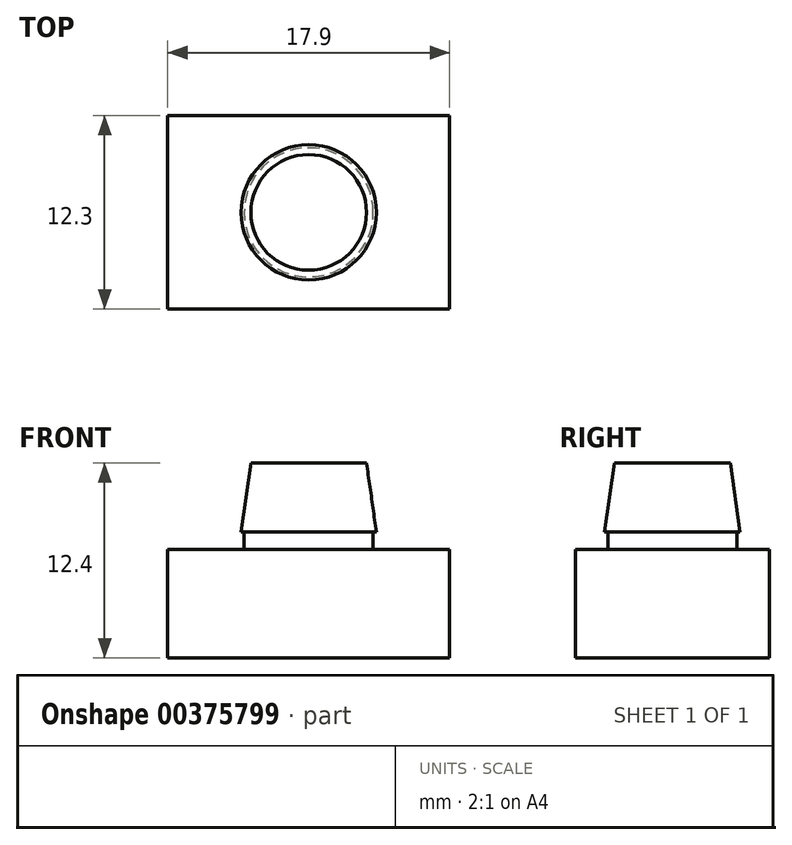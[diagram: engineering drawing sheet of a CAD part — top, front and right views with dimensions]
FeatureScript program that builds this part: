
annotation { "Feature Type Name" : "Feature", "Feature Type Description" : "" }
export const myFeature = defineFeature(function(context is Context, id is Id, definition is map)
    precondition{}
    {
        {
            var Q0;
            Q0=qCreatedBy(makeId("Top.planeOp"),FACE);
            var sketch = newSketch(context, id + "F0", { "sketchPlane" : qUnion([Q0])});
            skLineSegment(sketch, "E0.bottom", {"start": v(8.95, 6.15) * mm, "end": v(-8.95, 6.15) * mm});
            skLineSegment(sketch, "E0.top", {"start": v(8.95, -6.15) * mm, "end": v(-8.95, -6.15) * mm});
            skLineSegment(sketch, "E0.left", {"start": v(8.95, 6.15) * mm, "end": v(8.95, -6.15) * mm});
            skLineSegment(sketch, "E0.right", {"start": v(-8.95, 6.15) * mm, "end": v(-8.95, -6.15) * mm});
            skPoint(sketch, "E0.middle", {"position": v(0, 0) * mm});
            skSolve(sketch);
        }
        {
            var Q0;
            Q0 = qSketchRegion(id + "F0", true);
            extrude(context, id + "F1", {"entities" : qUnion([Q0]), "depth" : 6.9 * mm});
        }
        {
            var Q0;
            Q0=makeQuery(id+"F1.opExtrude","CAP_FACE",FACE,{"disambiguationData":[OSD([sQuery(id+"F0.wireOp",EDGE,"E0.bottom"),sQuery(id+"F0.wireOp",EDGE,"E0.top"),sQuery(id+"F0.wireOp",EDGE,"E0.left"),sQuery(id+"F0.wireOp",EDGE,"E0.right")])],"isStart":false});
            var sketch = newSketch(context, id + "F2", { "sketchPlane" : qUnion([Q0])});
            skCircle(sketch, "E1", {"center": v(0, 0) * mm, "radius": 4.1 * mm});
            skSolve(sketch);
        }
        {
            var Q0;
            Q0 = qSketchRegion(id + "F2", true);
            extrude(context, id + "F3", {"entities" : qUnion([Q0]), "operationType" : NewBodyOperationType.ADD, "depth" : 1.1 * mm});
        }
        {
            var Q0;
            Q0=makeQuery(id+"F3.opExtrude","CAP_FACE",FACE,{"disambiguationData":[OSD([sQuery(id+"F2.wireOp",EDGE,"E1")])],"isStart":false});
            var sketch = newSketch(context, id + "F4", { "sketchPlane" : qUnion([Q0])});
            skCircle(sketch, "E2", {"center": v(0, 0) * mm, "radius": 4.3 * mm});
            skSolve(sketch);
        }
        {
            var Q0;
            Q0=qCreatedBy(makeId("Front.planeOp"),FACE);
            var sketch = newSketch(context, id + "F5", { "sketchPlane" : qUnion([Q0])});
            skLineSegment(sketch, "E3", {"start": v(0, 0) * mm, "end": v(0, 12.4) * mm});
            skSolve(sketch);
        }
        {
            var Q0;
            Q0=sQuery(id+"F5.wireOp",VERTEX,"E3.end");
            var Q1;
            Q1=makeQuery(id+"F1.opExtrude","CAP_FACE",FACE,{"disambiguationData":[OSD([sQuery(id+"F0.wireOp",EDGE,"E0.bottom"),sQuery(id+"F0.wireOp",EDGE,"E0.top"),sQuery(id+"F0.wireOp",EDGE,"E0.left"),sQuery(id+"F0.wireOp",EDGE,"E0.right")])],"isStart":false});
            cPlane(context, id + "F6", {"entities" : qUnion([Q0, Q1]), "cplaneType" : CPlaneType.PLANE_POINT, "offset" : 25.4 * mm, "width" : 152.4 * mm, "height" : 152.4 * mm});
        }
        {
            var Q0;
            Q0=qCreatedBy(id+"F6.planeOp",FACE);
            var sketch = newSketch(context, id + "F7", { "sketchPlane" : qUnion([Q0])});
            skCircle(sketch, "E4", {"center": v(0, 0) * mm, "radius": 3.68 * mm});
            skSolve(sketch);
        }
        {
            var Q1;
            Q1 = qSketchRegion(id + "F7", true);
            var Q2;
            Q2 = qSketchRegion(id + "F4", true);
            loft(context, id + "F8", {"operationType" : NewBodyOperationType.ADD, "sheetProfilesArray" : [{ "sheetProfileEntities" : qUnion([Q1]) }, { "sheetProfileEntities" : qUnion([Q2]) }]});
        }
    });
